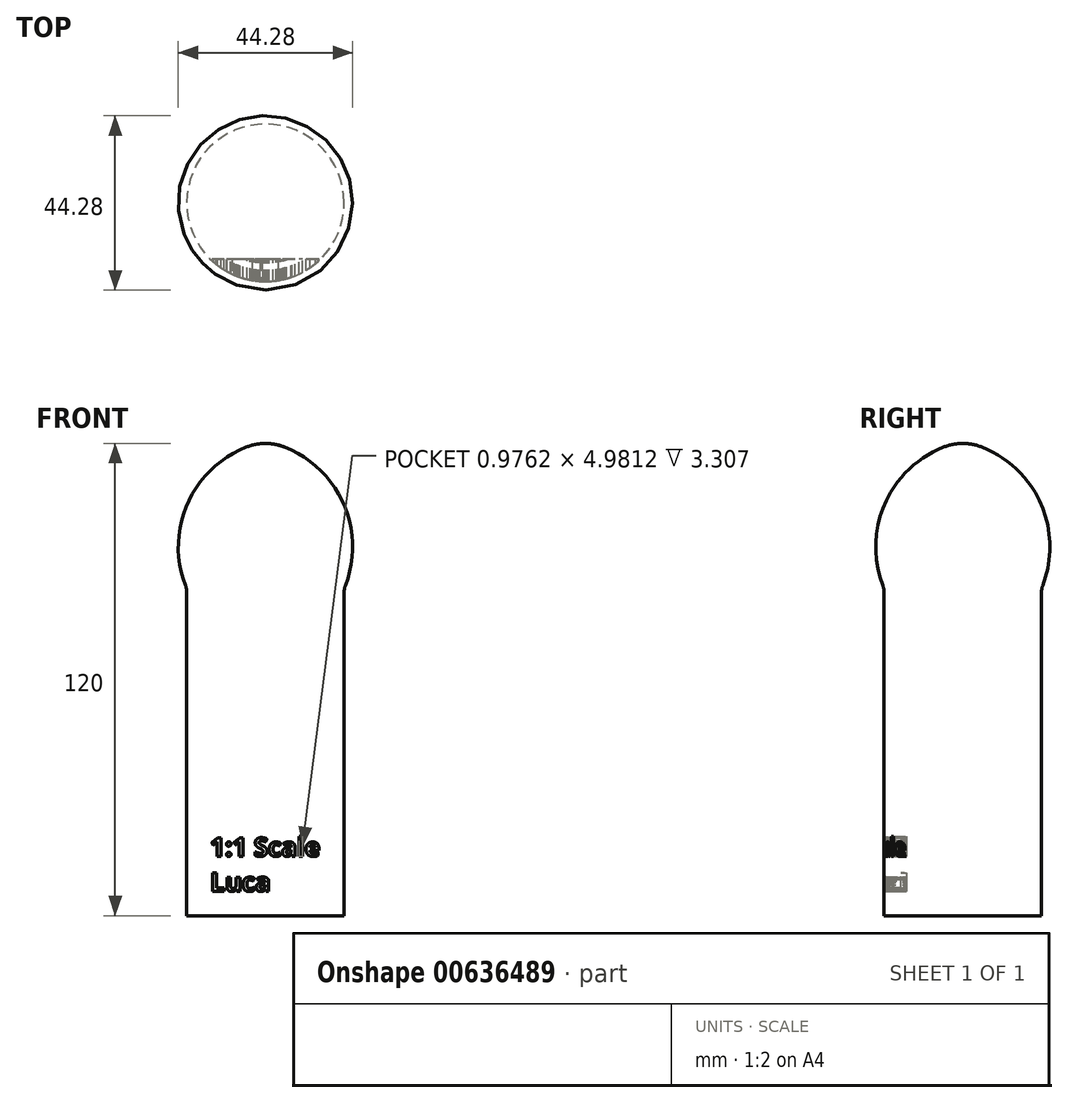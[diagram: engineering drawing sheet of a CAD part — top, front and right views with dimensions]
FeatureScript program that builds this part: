
annotation { "Feature Type Name" : "Feature", "Feature Type Description" : "" }
export const myFeature = defineFeature(function(context is Context, id is Id, definition is map)
    precondition{}
    {
        {
            var Q0;
            Q0=qCreatedBy(makeId("Front.planeOp"),FACE);
            var sketch = newSketch(context, id + "F0", { "sketchPlane" : qUnion([Q0])});
            skLineSegment(sketch, "E0", {"start": v(0, 0) * mm, "end": v(20, 0) * mm});
            skLineSegment(sketch, "E1", {"start": v(20, 0) * mm, "end": v(20, 83.15) * mm});
            skLineSegment(sketch, "E2", {"start": v(0, 120) * mm, "end": v(0, 0) * mm});
            skArc(sketch, "E3", {"start": v(4.9, 119.07) * mm, "mid": v(2.5, 119.77) * mm, "end": v(0, 120) * mm});
            skArc(sketch, "E4", {"start": v(20, 83.15) * mm, "mid": v(20, 104.29) * mm, "end": v(4.9, 119.07) * mm});
            skSolve(sketch);
        }
        {
            var Q0;
            Q0=makeQuery(id+"F0.imprint","IMPRINT",FACE,{"disambiguationData":[TD([[makeQuery(id+"F0.imprint","IMPRINT",EDGE,{"derivedFrom":sQuery(id+"F0.wireOp",EDGE,"E0")}),1.0]])]});
            var Q1;
            Q1=sQuery(id+"F0.wireOp",EDGE,"E2");
            revolve(context, id + "F1", {"entities" : qUnion([Q0]), "axis" : qUnion([Q1]), "revolveType" : RevolveType.FULL});
        }
        {
            var Q0;
            Q0=qCreatedBy(makeId("Front.planeOp"),FACE);
            cPlane(context, id + "F2", {"entities" : qUnion([Q0]), "cplaneType" : CPlaneType.OFFSET, "offset" : 14.3 * mm, "width" : 150 * mm, "height" : 150 * mm});
        }
        {
            var Q0;
            Q0=qCreatedBy(id+"F2.planeOp",FACE);
            var sketch = newSketch(context, id + "F3", { "sketchPlane" : qUnion([Q0])});
            skText(sketch, "E5", { "text": "1:1 Scale \nLuca ", "fontName": "OpenSans-Bold.ttf"});
            const initialGuessF3  = {"E5": [-0.014, 0.01513, 1, 0, 0.00472]};
            skSetInitialGuess(sketch, initialGuessF3);
            skSolve(sketch);
        }
        {
            var Q0;
            Q0 = qSketchRegion(id + "F3", true);
            extrude(context, id + "F4", {"entities" : qUnion([Q0]), "operationType" : NewBodyOperationType.REMOVE, "depth" : 25 * mm, "offsetDistance" : 25 * mm});
        }
        {
            var Q0;
            Q0=makeQuery(id+"F1.opRevolve","SWEPT_EDGE",EDGE,{"disambiguationData":[OSD([sQuery(id+"F0.wireOp",EDGE,"E1"),sQuery(id+"F0.wireOp",EDGE,"E4")])]});
            fillet(context, id + "F5", {"entities" : qUnion([Q0]), "radius" : 5 * mm, "tangentPropagation" : true, "allowEdgeOverflow" : false});
        }
    });
